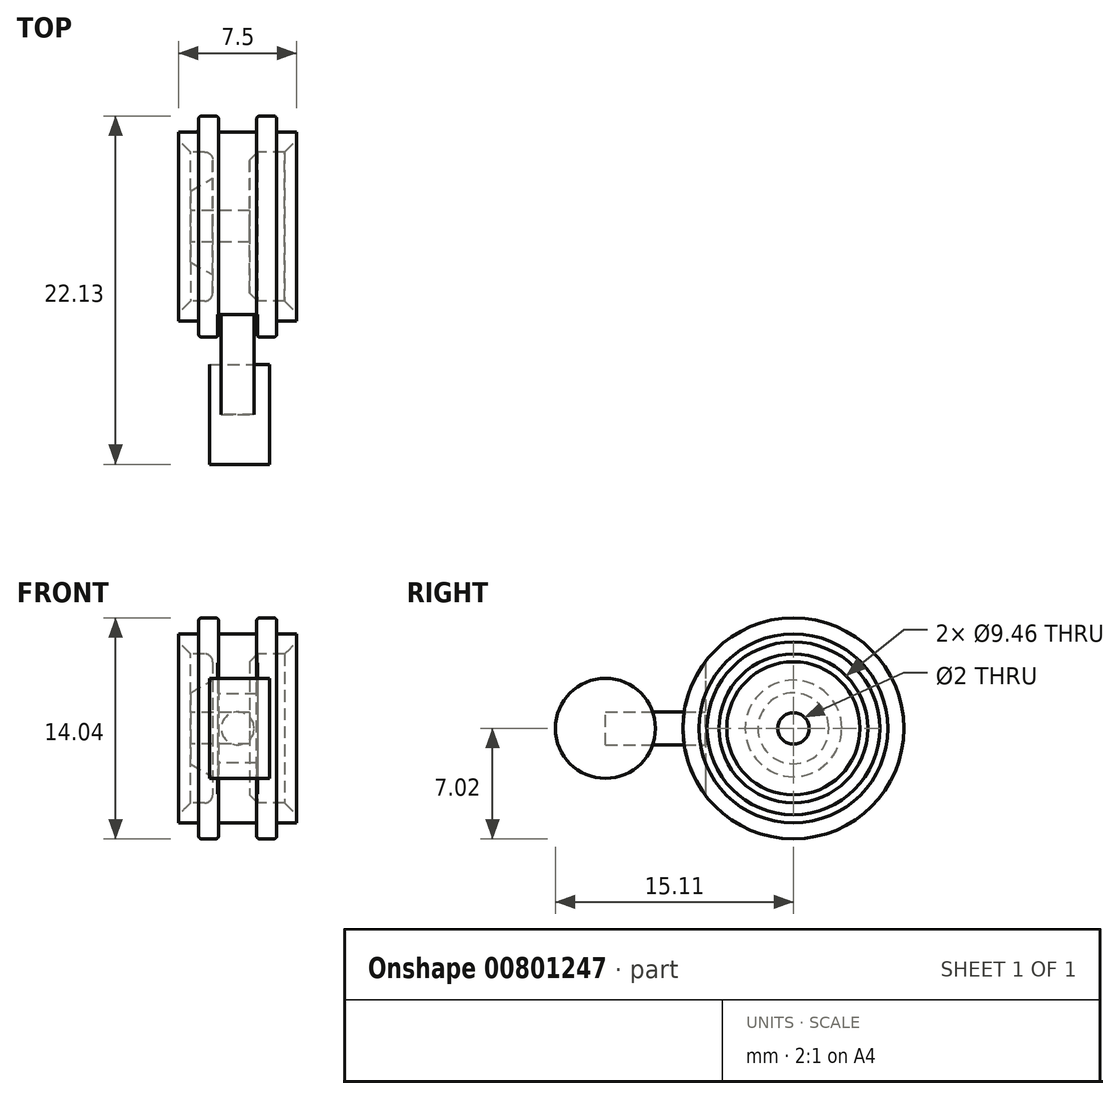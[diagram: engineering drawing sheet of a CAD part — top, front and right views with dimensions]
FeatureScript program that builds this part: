
annotation { "Feature Type Name" : "Feature", "Feature Type Description" : "" }
export const myFeature = defineFeature(function(context is Context, id is Id, definition is map)
    precondition{}
    {
        {
            var Q0;
            Q0=qCreatedBy(makeId("Front.planeOp"),FACE);
            var sketch = newSketch(context, id + "F0", { "sketchPlane" : qUnion([Q0])});
            skLineSegment(sketch, "E0", {"start": v(-3, 1) * mm, "end": v(0.76, 1) * mm});
            skLineSegment(sketch, "E1", {"start": v(0.76, 1) * mm, "end": v(0.76, 4.23) * mm});
            skLineSegment(sketch, "E2", {"start": v(1.26, 4.73) * mm, "end": v(3.75, 4.73) * mm});
            skLineSegment(sketch, "E3", {"start": v(3.75, 4.73) * mm, "end": v(3.75, 6) * mm});
            skLineSegment(sketch, "E4", {"start": v(3.75, 6) * mm, "end": v(2.48, 6) * mm});
            skLineSegment(sketch, "E5", {"start": v(2.48, 6) * mm, "end": v(2.48, 7.02) * mm});
            skLineSegment(sketch, "E6", {"start": v(2.48, 7.02) * mm, "end": v(1.2, 7.02) * mm});
            skLineSegment(sketch, "E7", {"start": v(-2.48, 7.02) * mm, "end": v(-2.48, 6) * mm});
            skLineSegment(sketch, "E8", {"start": v(-2.48, 6) * mm, "end": v(-3.75, 6) * mm});
            skLineSegment(sketch, "E9", {"start": v(-3.75, 6) * mm, "end": v(-3.75, 4.73) * mm});
            skLineSegment(sketch, "E10", {"start": v(-1.59, 3.07) * mm, "end": v(-3, 2.25) * mm});
            skLineSegment(sketch, "E11", {"start": v(-3, 2.25) * mm, "end": v(-3, 1) * mm});
            skLineSegment(sketch, "E12", {"start": v(0, 7.02) * mm, "end": v(0, 0) * mm, "construction": true});
            skLineSegment(sketch, "E13", {"start": v(0, 0) * mm, "end": v(34.63, 0) * mm});
            skLineSegment(sketch, "E14.left", {"start": v(-1.2, 7.02) * mm, "end": v(-1.2, 6) * mm});
            skLineSegment(sketch, "E14.right", {"start": v(1.2, 7.02) * mm, "end": v(1.2, 6) * mm});
            skLineSegment(sketch, "E15.trimOffspring", {"start": v(-1.2, 7.02) * mm, "end": v(-2.48, 7.02) * mm});
            skLineSegment(sketch, "E16", {"start": v(-1.59, 3.07) * mm, "end": v(-1.59, 4.23) * mm});
            skArc(sketch, "E17.filletArc", {"start": v(-1.59, 4.23) * mm, "mid": v(-1.73, 4.58) * mm, "end": v(-2.09, 4.73) * mm});
            skLineSegment(sketch, "E18", {"start": v(0.76, 4.23) * mm, "end": v(1.26, 4.73) * mm});
            skLineSegment(sketch, "E19", {"start": v(-1.2, 6) * mm, "end": v(1.2, 6) * mm});
            skLineSegment(sketch, "E20", {"start": v(-3.75, 5.37) * mm, "end": v(0, 5.37) * mm, "construction": true});
            skLineSegment(sketch, "E21", {"start": v(0, 5.37) * mm, "end": v(3.75, 5.37) * mm, "construction": true});
            skLineSegment(sketch, "E22", {"start": v(-1.2, 7.02) * mm, "end": v(0, 7.02) * mm, "construction": true});
            skLineSegment(sketch, "E23", {"start": v(0, 7.02) * mm, "end": v(1.2, 7.02) * mm, "construction": true});
            skLineSegment(sketch, "E24", {"start": v(-3.75, 4.73) * mm, "end": v(-2.09, 4.73) * mm});
            skSolve(sketch);
        }
        {
            var Q0;
            Q0 = qSketchRegion(id + "F0", true);
            var Q1;
            Q1=sQuery(id+"F0.wireOp",EDGE,"E13");
            revolve(context, id + "F1", {"surfaceOperationType" : NewSurfaceOperationType.NEW, "entities" : qUnion([Q0]), "axis" : qUnion([Q1]), "revolveType" : RevolveType.FULL});
        }
        {
            var Q0;
            Q0=makeQuery(id+"F1.opRevolve","SWEPT_EDGE",EDGE,{"disambiguationData":[OSD([sQuery(id+"F0.wireOp",EDGE,"E5"),sQuery(id+"F0.wireOp",EDGE,"E6")])]});
            var Q1;
            Q1=makeQuery(id+"F1.opRevolve","SWEPT_EDGE",EDGE,{"disambiguationData":[OSD([sQuery(id+"F0.wireOp",EDGE,"E6"),sQuery(id+"F0.wireOp",EDGE,"E7")])]});
            var Q2;
            Q2=makeQuery(id+"F1.opRevolve","SWEPT_EDGE",EDGE,{"disambiguationData":[OSD([sQuery(id+"F0.wireOp",EDGE,"E14.left"),sQuery(id+"F0.wireOp",EDGE,"E15.trimOffspring")])]});
            fillet(context, id + "F2", {"entities" : qUnion([Q0, Q1, Q2]), "radius" : 0.2 * mm, "tangentPropagation" : true, "allowEdgeOverflow" : false});
        }
        {
            var Q0;
            Q0=makeQuery(id+"F1.opRevolve","SWEPT_EDGE",EDGE,{"disambiguationData":[OSD([sQuery(id+"F0.wireOp",EDGE,"E2"),sQuery(id+"F0.wireOp",EDGE,"E3")])]});
            var Q1;
            Q1=makeQuery(id+"F1.opRevolve","SWEPT_EDGE",EDGE,{"disambiguationData":[OSD([sQuery(id+"F0.wireOp",EDGE,"E9"),sQuery(id+"F0.wireOp",EDGE,"E24")])]});
            chamfer(context, id + "F3", {"entities" : qUnion([Q0, Q1]), "width" : 0.76 * mm, "tangentPropagation" : true});
        }
        {
            var Q0;
            Q0=qCreatedBy(makeId("Right.planeOp"),FACE);
            var sketch = newSketch(context, id + "F4", { "sketchPlane" : qUnion([Q0])});
            skLineSegment(sketch, "E25.bottom", {"start": v(-10.48, 5.78) * mm, "end": v(-5.59, 5.78) * mm});
            skLineSegment(sketch, "E25.top", {"start": v(-10.48, -5.81) * mm, "end": v(-5.59, -5.81) * mm});
            skLineSegment(sketch, "E25.left", {"start": v(-10.48, 5.78) * mm, "end": v(-10.48, -5.81) * mm});
            skLineSegment(sketch, "E25.right", {"start": v(-5.59, 5.78) * mm, "end": v(-5.59, -5.81) * mm});
            skSolve(sketch);
        }
        {
            var Q0;
            Q0 = qSketchRegion(id + "F4", true);
            extrude(context, id + "F5", {"entities" : qUnion([Q0]), "operationType" : NewBodyOperationType.REMOVE, "oppositeDirection" : true, "depth" : 2.54 * mm, "offsetDistance" : 25.4 * mm, "symmetric" : true});
        }
        {
            var Q0;
            Q0=makeQuery(id+"F5.boolean.opBoolean","COPY",FACE,{"derivedFrom":makeQuery(id+"F5.opExtrude","SWEPT_FACE",FACE,{"disambiguationData":[OSD([sQuery(id+"F4.wireOp",EDGE,"E25.right")])]})});
            var sketch = newSketch(context, id + "F6", { "sketchPlane" : qUnion([Q0])});
            skCircle(sketch, "E26", {"center": v(0, 0) * mm, "radius": 1.05 * mm});
            skSolve(sketch);
        }
        {
            var Q0;
            Q0 = qSketchRegion(id + "F6", true);
            extrude(context, id + "F7", {"entities" : qUnion([Q0]), "operationType" : NewBodyOperationType.ADD, "depth" : 6.35 * mm, "offsetDistance" : 25.4 * mm});
        }
        {
            var Q0;
            Q0=makeQuery(id+"F7.opExtrude","CAP_FACE",FACE,{"disambiguationData":[OSD([sQuery(id+"F6.wireOp",EDGE,"E26")])],"isStart":false});
            var sketch = newSketch(context, id + "F8", { "sketchPlane" : qUnion([Q0])});
            skLineSegment(sketch, "E27", {"start": v(-1.05, 0) * mm, "end": v(1.05, 0) * mm});
            skSolve(sketch);
        }
        {
            var Q0;
            Q0=makeQuery(id+"F1.opRevolve","SWEPT_FACE",FACE,{"disambiguationData":[OSD([sQuery(id+"F0.wireOp",EDGE,"E1")])]});
            var sketch = newSketch(context, id + "F9", { "sketchPlane" : qUnion([Q0])});
            skCircle(sketch, "E28", {"center": v(-11.94, 0) * mm, "radius": 3.17 * mm});
            skLineSegment(sketch, "E29", {"start": v(-11.94, 0) * mm, "end": v(0, 0) * mm, "construction": true});
            skLineSegment(sketch, "E30", {"start": v(-11.94, 0) * mm, "end": v(-23.88, 0) * mm, "construction": true});
            skSolve(sketch);
        }
        {
            var Q0;
            Q0 = qSketchRegion(id + "F9", true);
            extrude(context, id + "F10", {"entities" : qUnion([Q0]), "oppositeDirection" : true, "depth" : 2.54 * mm, "offsetDistance" : 25.4 * mm, "hasSecondDirection" : true, "secondDirectionOppositeDirection" : false, "secondDirectionDepth" : 1.27 * mm});
        }
    });
